FCSTD DOCUMENT  (FreeCAD 0.18.4R)
Label: vigaRestricciones
License: All rights reserved
LicenseURL: http://en.wikipedia.org/wiki/All_rights_reserved
objects: Sketcher::SketchObject×1, PartDesign::Body×1
note: 2 computed .brp shape members not serialized (recipe doc carries the construction recipe); baked Part::Feature solids carry a one-line shape summary decoded from their .brp

FEATURE [Sketcher::SketchObject] Sketch
  MapMode = 5
  Support = -> [XY_Plane]
  sketch-geometry (14):
    g0: LineSegment StartX=1.8e-15 StartY=74 StartZ=0 EndX=90 EndY=74 EndZ=0
    g1: LineSegment StartX=90 StartY=74 StartZ=0 EndX=90 EndY=62 EndZ=0
    g2: LineSegment StartX=1.8e-15 StartY=74 StartZ=0 EndX=1.8e-15 EndY=62 EndZ=0
    g3: LineSegment StartX=1.8e-15 StartY=62 StartZ=0 EndX=30 EndY=62 EndZ=0
    g4: LineSegment StartX=60 StartY=62 StartZ=0 EndX=90 EndY=62 EndZ=0
    g5: LineSegment StartX=60 StartY=62 StartZ=0 EndX=60 EndY=12 EndZ=0
    g6: LineSegment StartX=30 StartY=62 StartZ=0 EndX=30 EndY=12 EndZ=0
    g7: LineSegment StartX=0 StartY=12 StartZ=0 EndX=30 EndY=12 EndZ=0
    g8: LineSegment StartX=0 StartY=12 StartZ=0 EndX=0 EndY=0 EndZ=0
    g9: LineSegment StartX=0 StartY=0 StartZ=0 EndX=90 EndY=0 EndZ=0
    g10: LineSegment StartX=90 StartY=12 StartZ=0 EndX=90 EndY=0 EndZ=0
    g11: LineSegment StartX=60 StartY=12 StartZ=0 EndX=90 EndY=12 EndZ=0
    g12: GeomPoint X=30 Y=12 Z=0
    g13: GeomPoint X=30 Y=12 Z=0
  constraints (37):
    c: Coincident(g0,g2)
    c: Coincident(g2,g3)
    c: Coincident(g3,g6)
    c: Coincident(g5,g4)
    c: Coincident(g4,g1)
    c: Coincident(g0,g1)
    c: Coincident(g7,g6)
    c: Coincident(g7,g8)
    c: Coincident(g8,g9)
    c: Coincident(g10,g9)
    c: Coincident(g10,g11)
    c: Coincident(g11,g5)
    c: Horizontal(g0)
    c: Horizontal(g9)
    c: Horizontal(g7)
    c: Horizontal(g11)
    c: Horizontal(g3)
    c: Horizontal(g4)
    c: Vertical(g1)
    c: Vertical(g2)
    c: Vertical(g8)
    c: Vertical(g10)
    c: Vertical(g5)
    c: Vertical(g6)
    c: Coincident(g6,g12)
    c: DistanceX(g9,g9) = 90
    c: DistanceX(g0,g0) = 90
    c: DistanceY(g1,g1) = 12
    c: DistanceY(g2,g2) = 12
    c: DistanceY(g10,g10) = 12
    c: DistanceY(g8,g8) = 12
    c: DistanceY(g6,g6) = 50
    c: DistanceX(g3,g3) = 30
    c: DistanceX(g4,g4) = 30
    c: DistanceX(g7,g7) = 30
    c: Coincident(g6,g13)
    c: Coincident(g8,g-1)
FEATURE [PartDesign::Body] Body
  Group = -> [Sketch]
  Origin = -> Origin
